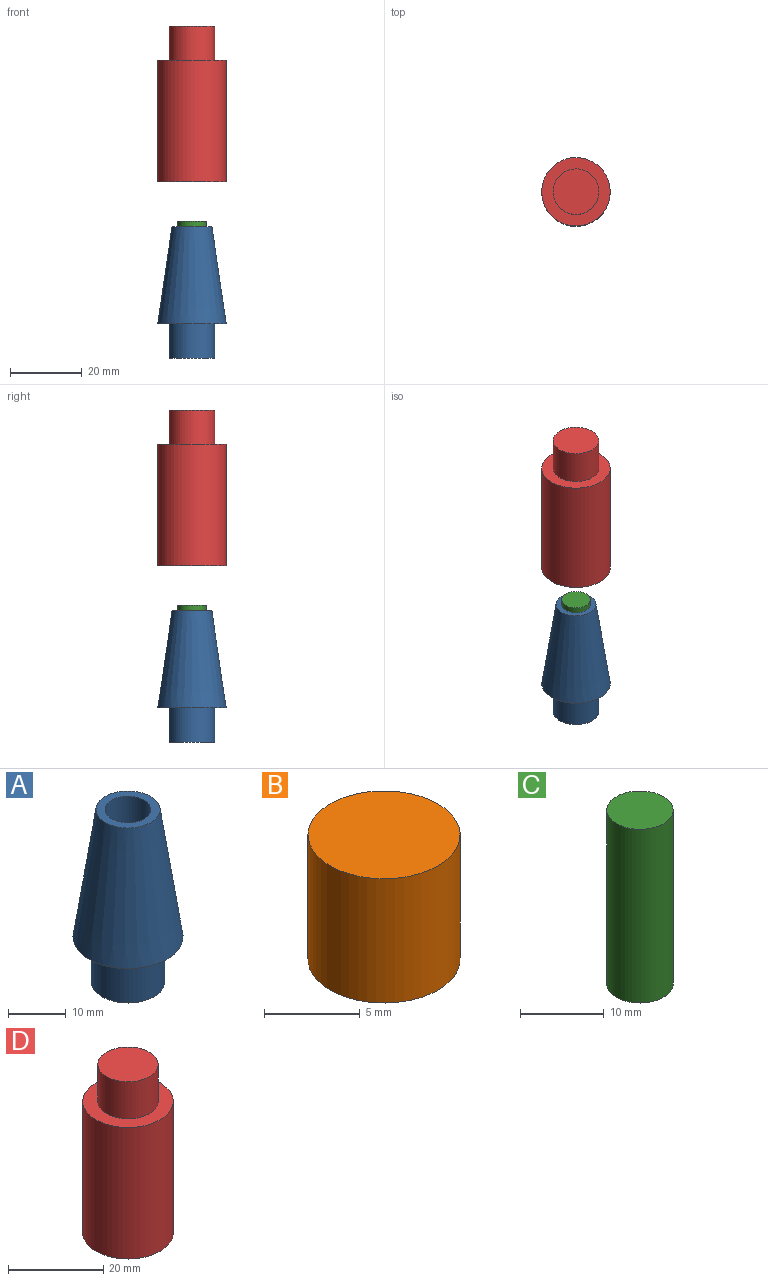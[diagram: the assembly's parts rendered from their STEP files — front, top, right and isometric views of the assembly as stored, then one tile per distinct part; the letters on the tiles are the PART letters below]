
ASSEMBLY  parts=4 mates=3
PART A: 7 faces, bbox 19.1x19.1x36.5 mm
  f0: plane 12.7x12.7mm, normal (0,0,-1), area 126.7mm2, adj f1
  f1: cylinder r=6.35mm len=12.7mm, axis (0,0,1), area 380mm2, adj f0,f2
  f2: plane 19.05x19.05mm, normal (0,0,-1), area 158.3mm2, adj f1,f3
  f3: cone r=9.53mm half-angle=8.4deg, axis (0,0,-1), area 1292.4mm2, adj f2,f4
  f4: plane 11.11x11.11mm, normal (0,0,1), area 47.5mm2, adj f3,f5
  f5: cylinder r=3.97mm len=23.81mm, axis (0,0,1), area 593.8mm2, adj f4,f6
  f6: plane 7.94x7.94mm, normal (0,0,1), area 49.5mm2, adj f5
PART B: 3 faces, bbox 7.9x7.9x7.9 mm
  f0: plane 7.94x7.94mm, normal (0,0,1), area 49.5mm2, adj f2
  f1: plane 7.94x7.94mm, normal (0,0,-1), area 49.5mm2, adj f2
  f2: cylinder r=3.97mm len=7.94mm, axis (0,0,1), area 197.9mm2, adj f0,f1
PART C: 3 faces, bbox 7.9x7.9x25.4 mm
  f0: plane 7.94x7.94mm, normal (0,0,-1), area 49.5mm2, adj f1
  f1: cylinder r=3.97mm len=25.4mm, axis (0,0,1), area 633.4mm2, adj f0,f2
  f2: plane 7.94x7.94mm, normal (0,0,1), area 49.5mm2, adj f1
PART D: 9 faces, bbox 19.1x19.1x43.4 mm
  f0: plane 19.05x19.05mm, normal (0,0,-1), area 45.5mm2, adj f1,f8
  f1: cylinder r=9.53mm len=33.86mm, axis (0,0,1), area 2026.3mm2, adj f0,f2
  f2: plane 19.05x19.05mm, normal (0,0,1), area 158.3mm2, adj f1,f3
  f3: cylinder r=6.35mm len=12.7mm, axis (0,0,1), area 380mm2, adj f2,f4
  f4: plane 12.7x12.7mm, normal (0,0,1), area 126.7mm2, adj f3
  f5: plane 7.94x7.94mm, normal (0,0,-1), area 49.5mm2, adj f6
  f6: cylinder r=3.97mm len=9.53mm, axis (0,0,1), area 237.5mm2, adj f5,f7
  f7: plane 11.24x11.24mm, normal (0,0,-1), area 49.7mm2, adj f6,f8
  f8: cone r=5.62mm half-angle=8.4deg, axis (0,0,-1), area 964.2mm2, adj f0,f7
PLACE A at identity
PLACE B t=(0,0,89.65)mm
PLACE C t=(0,0,65.01)mm
PLACE D t=(0,0,14.45)mm
MATE slider D.f1 <-> A.f1  axis (0,0,1) through (0,0,65.95)mm
MATE fastened B.f2 <-> D.f1  axis (0,0,1) through (0,0,79.7)mm
MATE fastened A.f1 <-> C.f1  axis (0,0,1) through (0,0,12.7)mm
